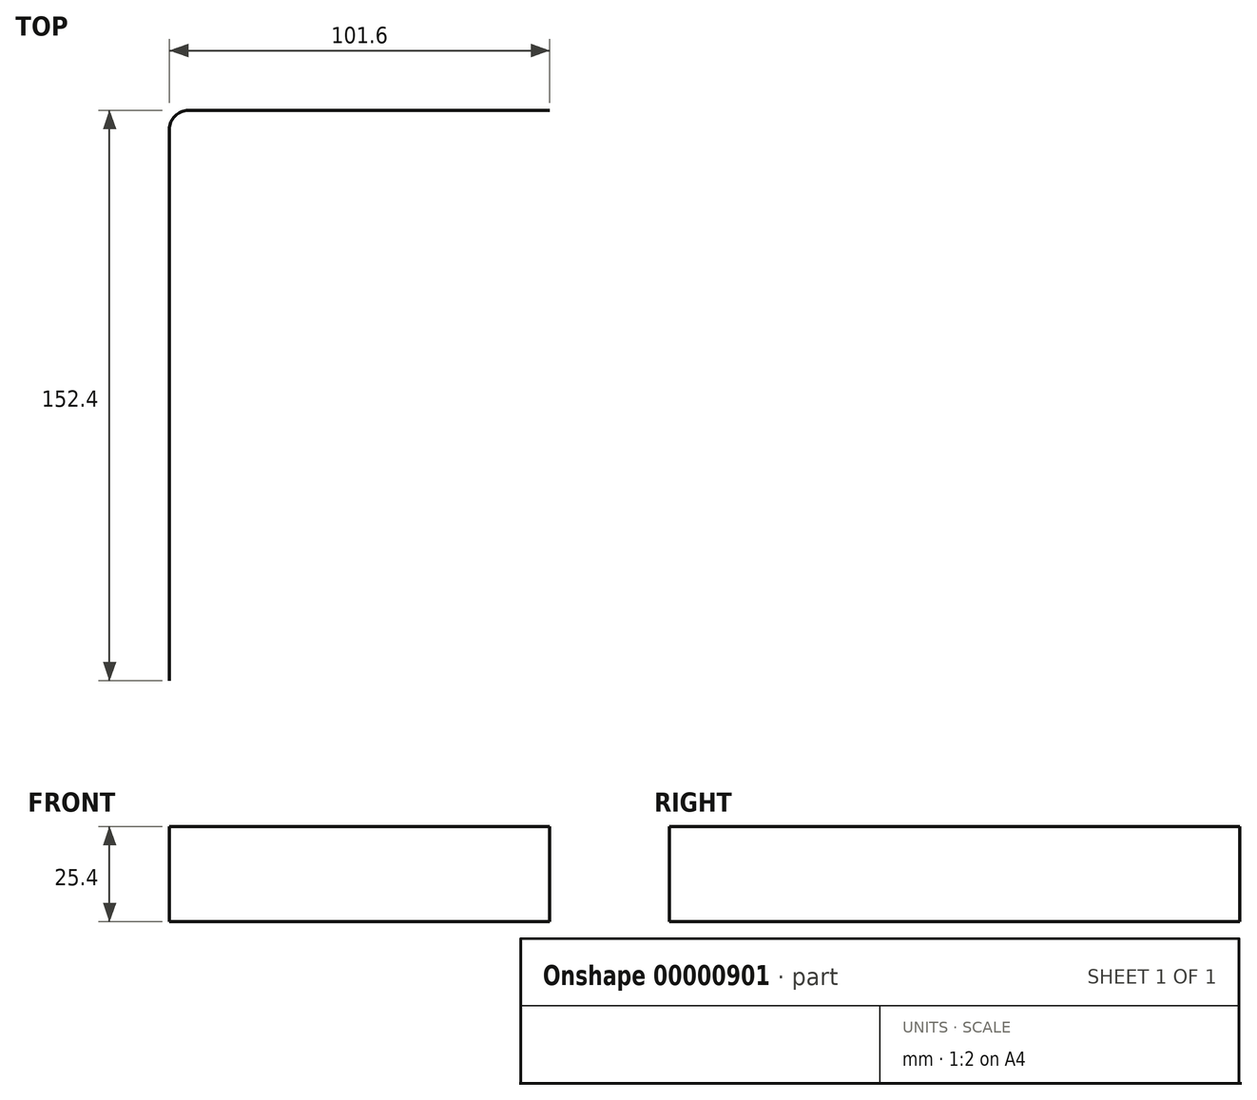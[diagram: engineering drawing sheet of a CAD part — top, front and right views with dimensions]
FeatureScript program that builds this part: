
annotation { "Feature Type Name" : "Feature", "Feature Type Description" : "" }
export const myFeature = defineFeature(function(context is Context, id is Id, definition is map)
    precondition{}
    {
        {
            var Q0;
            Q0=qCreatedBy(makeId("Top.planeOp"),FACE);
            var sketch = newSketch(context, id + "F0", { "sketchPlane" : qUnion([Q0])});
            skLineSegment(sketch, "E0", {"start": v(0, 0) * mm, "end": v(0, 152.4) * mm});
            skLineSegment(sketch, "E1", {"start": v(0, 152.4) * mm, "end": v(101.6, 152.4) * mm});
            skSolve(sketch);
        }
        {
            var Q0;
            Q0 = qSketchRegion(id + "F0", true);
            var Q1;
            Q1=sQuery(id+"F0.wireOp",EDGE,"E0");
            var Q2;
            Q2=sQuery(id+"F0.wireOp",EDGE,"E1");
            extrude(context, id + "F1", {"entities" : qUnion([Q0]), "bodyType" : ToolBodyType.SURFACE, "surfaceEntities" : qUnion([Q1, Q2]), "depth" : 25.4 * mm});
        }
        {
            var Q0;
            Q0=makeQuery(id+"F1.opExtrude","SWEPT_EDGE",EDGE,{"disambiguationData":[OSD([sQuery(id+"F0.wireOp",VERTEX,"E1.start")])]});
            fillet(context, id + "F2", {"entities" : qUnion([Q0]), "radius" : 5.08 * mm, "tangentPropagation" : true, "allowEdgeOverflow" : false});
        }
    });
